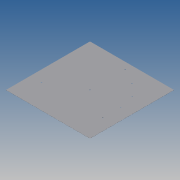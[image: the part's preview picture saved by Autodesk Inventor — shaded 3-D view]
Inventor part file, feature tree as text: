
AUTODESK INVENTOR PART (.ipt)
format: ipt  version: 2014 SP1 (Build 180222100, 222)  size: 140,800 bytes
history: native  units: in
note: dims shown in document units (in); Inventor stores cm internally (conversion verified against a paired STEP export)
features: extrude x2, sketch x2
ambient origin geometry x8: Origin, YZ Plane, XZ Plane, XY Plane, X Axis, Y Axis, Z Axis, Center Point
bodies: Solid1 (feature_tree)
feature tree (4):
  extrude  "outer"  Depth=787.4016in
  extrude  "polesPosts"  Depth=1.0in
  sketch  "Sketch1"  dims[d0=787.4016in d1=787.4016in]
  sketch  "Sketch2"  dims[d2=1.0in d3=0.0in d4=10.0in d5=10.0in d6=331.8898in d7=10.0in d8=289.3701in d9=1.1811in d11=360.0deg d13=1.1811in d15=60.0deg d17=1.0in d18=0.0in]
